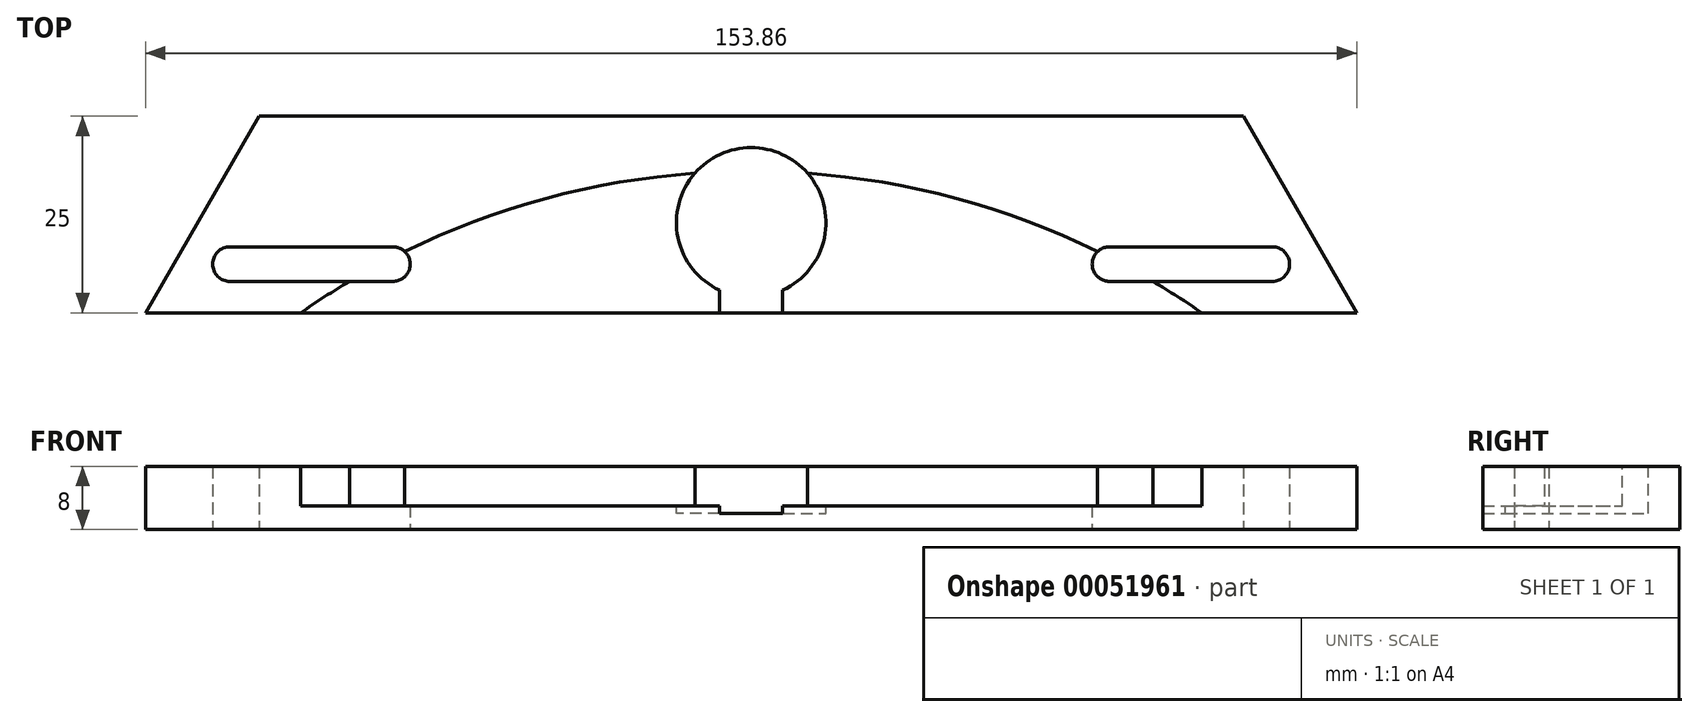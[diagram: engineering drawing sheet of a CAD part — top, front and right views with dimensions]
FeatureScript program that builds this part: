
annotation { "Feature Type Name" : "Feature", "Feature Type Description" : "" }
export const myFeature = defineFeature(function(context is Context, id is Id, definition is map)
    precondition{}
    {
        {
            var Q0;
            Q0=qCreatedBy(makeId("Top.planeOp"),FACE);
            var sketch = newSketch(context, id + "F0", { "sketchPlane" : qUnion([Q0])});
            skArc(sketch, "E0", {"start": v(90.5, 42.54) * mm, "mid": v(0, 100) * mm, "end": v(-90.5, 42.54) * mm});
            skLineSegment(sketch, "E1", {"start": v(-90.5, 42.54) * mm, "end": v(90.5, 42.54) * mm});
            skSolve(sketch);
        }
        {
            var Q0;
            Q0=makeQuery(id+"F0.imprint","IMPRINT",FACE,{"disambiguationData":[TD([[makeQuery(id+"F0.imprint","IMPRINT",EDGE,{"derivedFrom":sQuery(id+"F0.wireOp",EDGE,"E0")}),1.0]])]});
            cPlane(context, id + "F1", {"entities" : qUnion([Q0]), "cplaneType" : CPlaneType.OFFSET, "offset" : 3 * mm, "oppositeDirection" : true, "width" : 150 * mm, "height" : 150 * mm});
        }
        {
            var Q0;
            Q0=qCreatedBy(id+"F1.planeOp",FACE);
            var sketch = newSketch(context, id + "F2", { "sketchPlane" : qUnion([Q0])});
            skLineSegment(sketch, "E2.bottom", {"start": v(-62.5, 107) * mm, "end": v(62.5, 107) * mm});
            skLineSegment(sketch, "E2.top", {"start": v(-62.5, 82) * mm, "end": v(62.5, 82) * mm});
            skLineSegment(sketch, "E2.left", {"start": v(-62.5, 107) * mm, "end": v(-62.5, 82) * mm});
            skLineSegment(sketch, "E2.right", {"start": v(62.5, 107) * mm, "end": v(62.5, 82) * mm});
            skLineSegment(sketch, "E3", {"start": v(0, 0) * mm, "end": v(0, 282.76) * mm, "construction": true});
            skPoint(sketch, "E4", {"position": v(0, 82) * mm});
            skLineSegment(sketch, "E5", {"start": v(-62.5, 107) * mm, "end": v(-76.93, 82) * mm});
            skLineSegment(sketch, "E6", {"start": v(-76.93, 82) * mm, "end": v(-62.5, 82) * mm});
            skLineSegment(sketch, "E7.MirrorCS", {"start": v(62.5, 107) * mm, "end": v(76.93, 82) * mm});
            skLineSegment(sketch, "E8.MirrorCS", {"start": v(76.93, 82) * mm, "end": v(62.5, 82) * mm});
            skSolve(sketch);
        }
        {
            var Q0;
            Q0=qSketchRegion(id+"F2",true);
            extrude(context, id + "F3", {"entities" : qUnion([Q0]), "depth" : 8 * mm});
        }
        {
            var Q0;
            Q0=qSketchRegion(id+"F0",true);
            extrude(context, id + "F4", {"entities" : qUnion([Q0]), "operationType" : NewBodyOperationType.REMOVE, "depth" : 25 * mm});
        }
        {
            var Q0;
            Q0=qCreatedBy(makeId("Top.planeOp"),FACE);
            var sketch = newSketch(context, id + "F5", { "sketchPlane" : qUnion([Q0])});
            skArc(sketch, "E9", {"start": v(4, 84.88) * mm, "mid": v(0, 103) * mm, "end": v(-4, 84.88) * mm});
            skLineSegment(sketch, "E10", {"start": v(-4, 84.88) * mm, "end": v(-4, 82) * mm});
            skLineSegment(sketch, "E11", {"start": v(-4, 82) * mm, "end": v(4, 82) * mm});
            skLineSegment(sketch, "E12", {"start": v(4, 82) * mm, "end": v(4, 84.88) * mm});
            skSolve(sketch);
        }
        {
            var Q0;
            Q0=qSketchRegion(id+"F5",true);
            extrude(context, id + "F6", {"entities" : qUnion([Q0]), "operationType" : NewBodyOperationType.REMOVE, "oppositeDirection" : true, "depth" : 1 * mm, "hasSecondDirection" : true, "secondDirectionOppositeDirection" : false, "secondDirectionDepth" : 25 * mm});
        }
        {
            var Q0;
            Q0=makeQuery(id+"F3.opExtrude","CAP_FACE",FACE,{"disambiguationData":[OSD([sQuery(id+"F2.wireOp",EDGE,"E2.bottom"),sQuery(id+"F2.wireOp",EDGE,"E2.top"),sQuery(id+"F2.wireOp",EDGE,"E2.left"),sQuery(id+"F2.wireOp",EDGE,"E2.right")])],"isStart":false});
            var sketch = newSketch(context, id + "F7", { "sketchPlane" : qUnion([Q0])});
            skArc(sketch, "E13", {"start": v(58.77, 207) * mm, "mid": v(49.6, 196.07) * mm, "end": v(51.87, 182) * mm});
            skLineSegment(sketch, "E14", {"start": v(58.77, 207) * mm, "end": v(62.5, 207) * mm});
            skLineSegment(sketch, "E15", {"start": v(62.5, 207) * mm, "end": v(76.93, 182) * mm});
            skLineSegment(sketch, "E16", {"start": v(76.93, 182) * mm, "end": v(51.87, 182) * mm});
            skLineSegment(sketch, "E17.MirrorCS", {"start": v(-58.77, 207) * mm, "end": v(-62.5, 207) * mm});
            skLineSegment(sketch, "E18.MirrorCS", {"start": v(-62.5, 207) * mm, "end": v(-76.93, 182) * mm});
            skArc(sketch, "E19.MirrorCS", {"start": v(-58.77, 207) * mm, "mid": v(-49.6, 196.07) * mm, "end": v(-51.87, 182) * mm});
            skLineSegment(sketch, "E20.MirrorCS", {"start": v(-76.93, 182) * mm, "end": v(-51.87, 182) * mm});
            skSolve(sketch);
        }
        {
            var Q0;
            Q0=qSketchRegion(id+"F7",true);
            extrude(context, id + "F8", {"entities" : qUnion([Q0]), "operationType" : NewBodyOperationType.REMOVE, "oppositeDirection" : true, "depth" : 5 * mm});
        }
        {
            var Q0;
            Q0=qCreatedBy(id+"F1.planeOp",FACE);
            var sketch = newSketch(context, id + "F9", { "sketchPlane" : qUnion([Q0])});
            skArc(sketch, "E21", {"start": v(66.2, 86) * mm, "mid": v(68.4, 88.2) * mm, "end": v(66.2, 90.4) * mm});
            skLineSegment(sketch, "E22", {"start": v(55.86, 192.94) * mm, "end": v(55.86, 183.49) * mm, "construction": true});
            skLineSegment(sketch, "E23", {"start": v(66.2, 90.4) * mm, "end": v(55.86, 90.4) * mm});
            skLineSegment(sketch, "E24", {"start": v(66.2, 86) * mm, "end": v(55.86, 86) * mm});
            skArc(sketch, "E25.MirrorCS", {"start": v(45.52, 86) * mm, "mid": v(43.32, 88.2) * mm, "end": v(45.52, 90.4) * mm});
            skLineSegment(sketch, "E26.MirrorCS", {"start": v(45.52, 90.4) * mm, "end": v(55.86, 90.4) * mm});
            skLineSegment(sketch, "E27.MirrorCS", {"start": v(45.52, 86) * mm, "end": v(55.86, 86) * mm});
            skLineSegment(sketch, "E28.MirrorCS", {"start": v(-66.2, 86) * mm, "end": v(-55.86, 86) * mm});
            skLineSegment(sketch, "E29.MirrorCS", {"start": v(-66.2, 90.4) * mm, "end": v(-55.86, 90.4) * mm});
            skArc(sketch, "E30.MirrorCS", {"start": v(-45.52, 86) * mm, "mid": v(-43.32, 88.2) * mm, "end": v(-45.52, 90.4) * mm});
            skLineSegment(sketch, "E31.MirrorCS", {"start": v(-55.86, 192.94) * mm, "end": v(-55.86, 183.49) * mm, "construction": true});
            skArc(sketch, "E32.MirrorCS", {"start": v(-66.2, 86) * mm, "mid": v(-68.4, 88.2) * mm, "end": v(-66.2, 90.4) * mm});
            skLineSegment(sketch, "E33.MirrorCS", {"start": v(-45.52, 90.4) * mm, "end": v(-55.86, 90.4) * mm});
            skLineSegment(sketch, "E34.MirrorCS", {"start": v(-45.52, 86) * mm, "end": v(-55.86, 86) * mm});
            skSolve(sketch);
        }
        {
            var Q0;
            Q0=qSketchRegion(id+"F9",true);
            extrude(context, id + "F10", {"entities" : qUnion([Q0]), "operationType" : NewBodyOperationType.REMOVE, "depth" : 25 * mm});
        }
    });
